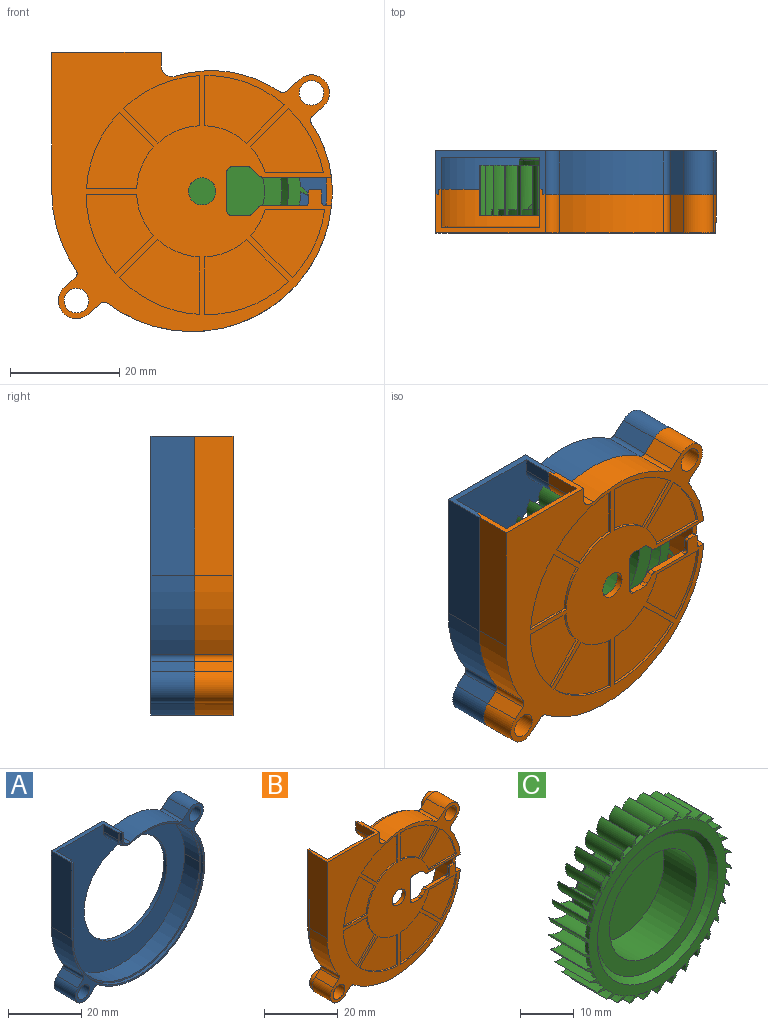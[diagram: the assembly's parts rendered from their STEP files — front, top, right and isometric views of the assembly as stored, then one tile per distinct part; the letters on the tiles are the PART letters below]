
ASSEMBLY  parts=3 mates=2
PART A: 35 faces, bbox 51.3x8x51.1 mm
  f0: cylinder r=25.15mm len=50.3mm, axis (0,-1,0), area 79mm2, adj f28,f32,f33,f34
  f1: cylinder r=2.5mm len=3.25mm, axis (0,-1,0), area 4.7mm2, adj f28,f31,f32,f34
  f2: cylinder r=2.25mm len=8mm, axis (0,1,0), area 113.1mm2, adj f28,f29
  f3: cylinder r=2.25mm len=8mm, axis (0,1,0), area 113.1mm2, adj f28,f29
  f4: cylinder r=22.07mm len=19.05mm, axis (0,1,0), area 159.4mm2, adj f20,f21,f28,f29
  f5: cylinder r=3.3mm len=8mm, axis (0,1,0), area 82.9mm2, adj f18,f19,f28,f29
  f6: cylinder r=1mm len=8mm, axis (0,1,0), area 11mm2, adj f14,f15,f28,f29
  f7: cylinder r=16mm len=32mm, axis (0,1,0), area 120.6mm2, adj f29,f30
  f8: cylinder r=24.65mm len=49.3mm, axis (0,-1,0), area 449.3mm2, adj f11,f12,f30,f34
  f9: cylinder r=3mm len=5.8mm, axis (0,-1,0), area 32.6mm2, adj f10,f11,f30,f34
  f10: plane 5.8x2.44mm, normal (-1,0,0), area 14.2mm2, adj f9,f23,f30,f34
  f11: cylinder r=21.07mm len=27.4mm, axis (0,-1,0), area 229.2mm2, adj f8,f9,f30,f34
  f12: plane 25.4x5.8mm, normal (1,0,0), area 147.3mm2, adj f8,f23,f30,f34
  f13: cylinder r=3.3mm len=8mm, axis (0,1,0), area 82.9mm2, adj f14,f27,f28,f29
  f14: plane 8x2.22mm, normal (0.66,0,-0.75), area 23.7mm2, adj f6,f13,f28,f29
  f15: cylinder r=25.65mm len=41.13mm, axis (0,1,0), area 455.4mm2, adj f6,f16,f28,f29
  f16: cylinder r=22.07mm len=12.41mm, axis (0,1,0), area 105.5mm2, adj f15,f17,f28,f29
  f17: cylinder r=1mm len=8mm, axis (0,1,0), area 11.6mm2, adj f16,f18,f28,f29
  f18: plane 8x2.04mm, normal (0.66,0,-0.75), area 21.8mm2, adj f5,f17,f28,f29
  f19: plane 8x2.44mm, normal (-0.66,0,0.75), area 26mm2, adj f5,f20,f28,f29
  f20: cylinder r=1mm len=8mm, axis (0,1,0), area 10.6mm2, adj f4,f19,f28,f29
  f21: cylinder r=2mm len=8mm, axis (0,1,0), area 30mm2, adj f4,f22,f28,f29
  f22: plane 8x2.44mm, normal (1,0,0), area 19.6mm2, adj f21,f23,f28,f29
  f23: plane 20x8mm, normal (0,0,1), area 36.6mm2, adj f10,f12,f22,f24,f28,f29,f30,f31
  f24: plane 25.4x8mm, normal (-1,0,0), area 203.2mm2, adj f23,f25,f28,f29
  f25: cylinder r=25.65mm len=14.47mm, axis (0,1,0), area 122.9mm2, adj f24,f26,f28,f29
  f26: cylinder r=1mm len=8mm, axis (0,1,0), area 11.6mm2, adj f25,f27,f28,f29
  f27: plane 8x1.98mm, normal (-0.66,0,0.75), area 21.1mm2, adj f13,f26,f28,f29
  f28: plane 51.3x51.07mm, normal (0,-1,0), area 126.8mm2, adj f0,f1,f2,f3,f4,f5,f6,f13
  f29: plane 51.3x51.07mm, normal (0,1,0), area 1370.5mm2, adj f2,f3,f4,f5,f6,f7,f13,f14
  f30: plane 50.07x49.3mm, normal (0,-1,0), area 1168mm2, adj f7,f8,f9,f10,f11,f12,f23
  f31: plane 2.44x1mm, normal (-1,0,0), area 2.4mm2, adj f1,f23,f28,f34
  f32: cylinder r=21.57mm len=28.05mm, axis (0,-1,0), area 40.5mm2, adj f0,f1,f28,f34
  f33: plane 25.4x1mm, normal (1,0,0), area 25.4mm2, adj f0,f23,f28,f34
  f34: plane 50.57x50.3mm, normal (0,-1,0), area 75.6mm2, adj f0,f1,f8,f9,f10,f11,f12,f23
PART B: 104 faces, bbox 52.9x8.5x51.4 mm
  f0: torus R=1.41mm, axis (0,-1,0), area 1.6mm2, adj f31,f35,f102,f103
  f1: cylinder r=21.88mm len=15.3mm, axis (0,-1,0), area 8.4mm2, adj f14,f53,f54,f55
  f2: cylinder r=2.82mm len=5.65mm, axis (0,-1,0), area 26.6mm2, adj f15,f41
  f3: cylinder r=2.82mm len=5.65mm, axis (0,-1,0), area 26.6mm2, adj f15,f40
  f4: cylinder r=21.57mm len=28.05mm, axis (0,1,0), area 40.5mm2, adj f15,f16,f37,f38
  f5: cylinder r=21.07mm len=27.4mm, axis (0,1,0), area 266.7mm2, adj f16,f31,f33,f34,f86,f87
  f6: cylinder r=2.5mm len=5mm, axis (0,-1,0), area 18.8mm2, adj f14,f31
  f7: cylinder r=2.25mm len=8.5mm, axis (0,-1,0), area 120.2mm2, adj f14,f40
  f8: cylinder r=2.25mm len=8.5mm, axis (0,-1,0), area 120.2mm2, adj f14,f41
  f9: cylinder r=25.65mm len=41.13mm, axis (0,-1,0), area 393.3mm2, adj f13,f14,f15,f28,f29,f87
  f10: cylinder r=1mm len=7mm, axis (0,-1,0), area 9.3mm2, adj f14,f15,f23,f24
  f11: cylinder r=2mm len=7mm, axis (0,-1,0), area 26.3mm2, adj f14,f15,f22,f23
  f12: cylinder r=3.3mm len=7mm, axis (0,-1,0), area 72.6mm2, adj f14,f15,f17,f30
  f13: plane 12.66x2mm, normal (0,0,1), area 13.2mm2, adj f9,f14,f31,f34,f87,f93,f95,f98
  f14: plane 51.17x51.07mm, normal (0,-1,0), area 1131.7mm2, adj f1,f6,f7,f8,f9,f10,f11,f12
  f15: plane 51.3x51.07mm, normal (0,1,0), area 108.5mm2, adj f2,f3,f4,f9,f10,f11,f12,f17
  f16: plane 50.57x50.3mm, normal (0,1,0), area 75.6mm2, adj f4,f5,f21,f32,f33,f34,f35,f36
  f17: plane 7x1.98mm, normal (-0.66,0,0.75), area 18.5mm2, adj f12,f14,f15,f18
  f18: cylinder r=1mm len=7mm, axis (0,-1,0), area 10.1mm2, adj f14,f15,f17,f19
  f19: cylinder r=25.65mm len=14.47mm, axis (0,-1,0), area 107.6mm2, adj f14,f15,f18,f20
  f20: plane 25.4x7mm, normal (-1,0,0), area 177.8mm2, adj f14,f15,f19,f21
  f21: plane 20x8mm, normal (0,0,1), area 31.2mm2, adj f14,f15,f16,f20,f22,f32,f35,f36
  f22: plane 7x2.44mm, normal (1,0,0), area 17.1mm2, adj f11,f14,f15,f21
  f23: cylinder r=22.07mm len=19.05mm, axis (0,-1,0), area 139.5mm2, adj f10,f11,f14,f15
  f24: plane 7x2.44mm, normal (-0.66,0,0.75), area 22.8mm2, adj f10,f14,f15,f25
  f25: cylinder r=3.3mm len=7mm, axis (0,-1,0), area 72.6mm2, adj f14,f15,f24,f26
  f26: plane 7x2.04mm, normal (0.66,0,-0.75), area 19.1mm2, adj f14,f15,f25,f27
  f27: cylinder r=1mm len=7mm, axis (0,-1,0), area 10.1mm2, adj f14,f15,f26,f28
  f28: cylinder r=22.07mm len=12.41mm, axis (0,-1,0), area 87.1mm2, adj f9,f14,f15,f27,f86,f87
  f29: cylinder r=1mm len=7mm, axis (0,-1,0), area 9.6mm2, adj f9,f14,f15,f30
  f30: plane 7x2.22mm, normal (0.66,0,-0.75), area 20.7mm2, adj f12,f14,f15,f29
  f31: plane 49.16x46.35mm, normal (0,1,0), area 1650.7mm2, adj f0,f5,f6,f13,f33,f34,f35,f81
  f32: plane 7.1x2.44mm, normal (-1,0,0), area 17.4mm2, adj f16,f21,f33,f102
  f33: cylinder r=3mm len=7.1mm, axis (0,1,0), area 38.5mm2, adj f5,f16,f31,f32,f103
  f34: cylinder r=24.65mm len=49.3mm, axis (0,1,0), area 524.7mm2, adj f5,f13,f16,f31,f35,f87
  f35: plane 25.4x7.1mm, normal (1,0,0), area 179.6mm2, adj f0,f16,f21,f31,f34,f102
  f36: plane 25.4x1mm, normal (-1,0,0), area 25.4mm2, adj f15,f16,f21,f37
  f37: cylinder r=25.15mm len=50.3mm, axis (0,1,0), area 79mm2, adj f4,f15,f16,f36
  f38: cylinder r=2.5mm len=3.25mm, axis (0,1,0), area 4.7mm2, adj f4,f15,f16,f39
  f39: plane 2.44x1mm, normal (1,0,0), area 2.4mm2, adj f15,f16,f21,f38
  f40: plane 5.65x5.65mm, normal (0,1,0), area 9.2mm2, adj f3,f7
  f41: plane 5.65x5.65mm, normal (0,1,0), area 9.2mm2, adj f2,f8
  f42: plane 6.99x6.99mm, normal (0.71,0,-0.71), area 4.9mm2, adj f14,f43,f45,f46
  f43: cylinder r=12mm len=7.62mm, axis (0,-1,0), area 4.2mm2, adj f14,f42,f44,f46
  f44: plane 10.54x0.5mm, normal (-1,0,0), area 5.3mm2, adj f14,f43,f45,f46
  f45: cylinder r=21.88mm len=14.61mm, axis (0,-1,0), area 8.2mm2, adj f14,f42,f44,f46
  f46: plane 14.61x13.7mm, normal (0,-1,0), area 127.2mm2, adj f42,f43,f44,f45
  f47: plane 7.67x7.67mm, normal (0.71,0,0.71), area 5.4mm2, adj f14,f48,f50,f51
  f48: cylinder r=12mm len=4.77mm, axis (0,-1,0), area 2.8mm2, adj f14,f47,f49,f51
  f49: plane 10.88x0.5mm, normal (0,0,-1), area 5.4mm2, adj f14,f48,f50,f51
  f50: cylinder r=21.88mm len=12.45mm, axis (0,-1,0), area 7mm2, adj f14,f47,f49,f51
  f51: plane 13.57x12.45mm, normal (0,-1,0), area 105.4mm2, adj f47,f48,f49,f50
  f52: cylinder r=12mm len=7.62mm, axis (0,-1,0), area 4.2mm2, adj f14,f53,f54,f55
  f53: plane 7.67x7.67mm, normal (-0.71,0,-0.71), area 5.4mm2, adj f1,f14,f52,f55
  f54: plane 10.57x0.5mm, normal (1,0,0), area 5.3mm2, adj f1,f14,f52,f55
  f55: plane 15.3x13.73mm, normal (0,-1,0), area 135.9mm2, adj f1,f52,f53,f54
  f56: cylinder r=12mm len=7.62mm, axis (0,-1,0), area 4.2mm2, adj f14,f57,f59,f60
  f57: plane 9.2x0.5mm, normal (1,0,0), area 4.6mm2, adj f14,f56,f58,f60
  f58: cylinder r=21.88mm len=14.58mm, axis (0,-1,0), area 7.9mm2, adj f14,f57,f59,f60
  f59: plane 6.96x6.96mm, normal (-0.71,0,0.71), area 4.9mm2, adj f14,f56,f58,f60
  f60: plane 14.58x12.36mm, normal (0,-1,0), area 115.4mm2, adj f56,f57,f58,f59
  f61: cylinder r=12mm len=4.77mm, axis (0,-1,0), area 2.8mm2, adj f14,f62,f64,f65
  f62: plane 6.99x6.99mm, normal (0.71,0,-0.71), area 4.9mm2, adj f14,f61,f63,f65
  f63: cylinder r=21.88mm len=11.76mm, axis (0,-1,0), area 6.8mm2, adj f14,f62,f64,f65
  f64: plane 10.66x0.5mm, normal (0,0,1), area 5.3mm2, adj f14,f61,f63,f65
  f65: plane 13.36x11.76mm, normal (0,-1,0), area 97mm2, adj f61,f62,f63,f64
  f66: cylinder r=12mm len=7.62mm, axis (0,-1,0), area 4.2mm2, adj f14,f67,f69,f70
  f67: plane 9.17x0.5mm, normal (0,0,1), area 4.6mm2, adj f14,f66,f68,f70
  f68: cylinder r=21.88mm len=13.93mm, axis (0,-1,0), area 7.7mm2, adj f14,f67,f69,f70
  f69: plane 6.3x6.3mm, normal (-0.71,0,-0.71), area 4.5mm2, adj f14,f66,f68,f70
  f70: plane 13.93x12.33mm, normal (0,-1,0), area 107.6mm2, adj f66,f67,f68,f69
  f71: plane 9.17x0.5mm, normal (-1,0,0), area 4.6mm2, adj f14,f72,f74,f75
  f72: cylinder r=12mm len=7.62mm, axis (0,-1,0), area 4.2mm2, adj f14,f71,f73,f75
  f73: plane 6.3x6.3mm, normal (0.71,0,0.71), area 4.5mm2, adj f14,f72,f74,f75
  f74: cylinder r=21.88mm len=13.93mm, axis (0,-1,0), area 7.7mm2, adj f14,f71,f73,f75
  f75: plane 13.93x12.33mm, normal (0,-1,0), area 107.6mm2, adj f71,f72,f73,f74
  f76: cylinder r=12mm len=7.62mm, axis (0,-1,0), area 4.2mm2, adj f14,f77,f79,f80
  f77: plane 6.96x6.96mm, normal (-0.71,0,0.71), area 4.9mm2, adj f14,f76,f78,f80
  f78: cylinder r=21.88mm len=14.58mm, axis (0,-1,0), area 7.9mm2, adj f14,f77,f79,f80
  f79: plane 9.2x0.5mm, normal (0,0,-1), area 4.6mm2, adj f14,f76,f78,f80
  f80: plane 14.58x12.36mm, normal (0,-1,0), area 115.4mm2, adj f76,f77,f78,f79
  f81: plane 1.31x1.31mm, normal (-0.71,0,0.71), area 2.2mm2, adj f14,f31,f92,f93
  f82: plane 2.79x1.2mm, normal (0,0,1), area 3.3mm2, adj f14,f31,f91,f92
  f83: plane 7x1.2mm, normal (1,0,0), area 8.4mm2, adj f14,f31,f88,f91
  f84: plane 2.79x1.2mm, normal (0,0,-1), area 3.3mm2, adj f14,f31,f88,f90
  f85: plane 1.31x1.31mm, normal (-0.71,0,-0.71), area 2.2mm2, adj f14,f31,f89,f90
  f86: plane 12.63x2mm, normal (0,0,-1), area 16mm2, adj f5,f14,f28,f31,f87,f89
  f87: plane 5.2x1.16mm, normal (0,-1,0), area 5.2mm2, adj f5,f9,f13,f28,f34,f86
  f88: cylinder r=1mm len=1.2mm, axis (0,1,0), area 1.9mm2, adj f14,f31,f83,f84
  f89: cylinder r=1mm len=1.2mm, axis (0,-1,0), area 0.9mm2, adj f14,f31,f85,f86
  f90: cylinder r=1mm len=1.2mm, axis (0,1,0), area 0.9mm2, adj f14,f31,f84,f85
  f91: cylinder r=1mm len=1.2mm, axis (0,1,0), area 1.9mm2, adj f14,f31,f82,f83
  f92: cylinder r=1mm len=1.2mm, axis (0,1,0), area 0.9mm2, adj f14,f31,f81,f82
  f93: cylinder r=1mm len=1.2mm, axis (0,-1,0), area 0.9mm2, adj f13,f14,f31,f81
  f94: plane 2x0.8mm, normal (1,0,0), area 1.6mm2, adj f14,f95,f100,f101
  f95: plane 3.5x3mm, normal (0,1,0), area 7.5mm2, adj f13,f94,f96,f97,f98,f99,f100,f101
  f96: plane 2x0.8mm, normal (-1,0,0), area 1.6mm2, adj f14,f95,f98,f99
  f97: plane 1.5x0.8mm, normal (0,0,1), area 1.2mm2, adj f14,f95,f99,f100
  f98: cylinder r=0.5mm len=0.8mm, axis (0,1,0), area 0.6mm2, adj f13,f14,f95,f96
  f99: cylinder r=0.5mm len=0.8mm, axis (0,1,0), area 0.6mm2, adj f14,f95,f96,f97
  f100: cylinder r=0.5mm len=0.8mm, axis (0,-1,0), area 0.6mm2, adj f14,f94,f95,f97
  f101: cylinder r=0.5mm len=0.8mm, axis (0,-1,0), area 0.6mm2, adj f13,f14,f94,f95
  f102: plane 22.44x18mm, normal (0,1,0), area 150.3mm2, adj f0,f21,f32,f35,f103
  f103: torus R=22.35mm, axis (0,1,0), area 37.3mm2, adj f0,f31,f33,f102
PART C: 207 faces, bbox 39x10.5x38.9 mm
  f0: cylinder r=11.4mm len=22.8mm, axis (0,-1,0), area 608.8mm2, adj f205,f206
  f1: cone r=14.6mm half-angle=45deg, axis (0,-1,0), area 162.1mm2, adj f119,f205
  f2: cylinder r=2.92mm len=9.2mm, axis (0,-1,0), area 52mm2, adj f85,f86,f87,f119,f143,f144
  f3: cylinder r=2.92mm len=9.2mm, axis (0,-1,0), area 52mm2, adj f88,f89,f90,f119,f141,f142
  f4: cylinder r=2.92mm len=9.2mm, axis (0,-1,0), area 52mm2, adj f91,f92,f93,f119,f139,f140
  f5: cylinder r=5.73mm len=9.2mm, axis (0,-1,0), area 44mm2, adj f6,f91,f92,f93,f119,f138
  f6: cylinder r=2.92mm len=9.2mm, axis (0,-1,0), area 52mm2, adj f5,f94,f95,f96,f119,f138
  f7: cylinder r=5.73mm len=9.2mm, axis (0,-1,0), area 44mm2, adj f8,f94,f95,f96,f119,f137
  f8: cylinder r=2.92mm len=9.2mm, axis (0,-1,0), area 52mm2, adj f7,f97,f98,f99,f119,f137
  f9: cylinder r=5.73mm len=9.2mm, axis (0,-1,0), area 44mm2, adj f10,f97,f98,f99,f119,f136
  f10: cylinder r=2.92mm len=9.2mm, axis (0,-1,0), area 52mm2, adj f9,f100,f101,f102,f119,f136
  f11: cylinder r=5.73mm len=9.2mm, axis (0,-1,0), area 44mm2, adj f12,f100,f101,f102,f119,f135
  f12: cylinder r=2.92mm len=9.2mm, axis (0,-1,0), area 52mm2, adj f11,f103,f104,f105,f119,f135
  f13: cylinder r=5.73mm len=9.2mm, axis (0,-1,0), area 44mm2, adj f14,f103,f104,f105,f119,f134
  f14: cylinder r=2.92mm len=9.2mm, axis (0,-1,0), area 52mm2, adj f13,f106,f107,f108,f119,f134
  f15: cylinder r=2.92mm len=9.2mm, axis (0,-1,0), area 52mm2, adj f109,f110,f111,f119,f132,f133
  f16: cylinder r=2.92mm len=9.2mm, axis (0,-1,0), area 52mm2, adj f112,f113,f114,f119,f130,f131
  f17: cylinder r=2.92mm len=9.2mm, axis (0,-1,0), area 52mm2, adj f115,f116,f117,f119,f128,f129
  f18: torus R=11.75mm, axis (0,1,0), area 59.6mm2, adj f19,f121
  f19: cylinder r=12.25mm len=24.5mm, axis (0,-1,0), area 577.3mm2, adj f18,f120
  f20: cone r=14.5mm half-angle=45deg, axis (0,-1,0), area 5.5mm2, adj f118,f120,f123,f125
  f21: cylinder r=18mm len=2.51mm, axis (0,-1,0), area 2.5mm2, adj f118,f119,f123,f125
  f22: cylinder r=18mm len=2.35mm, axis (0,-1,0), area 2.5mm2, adj f24,f119,f200,f202
  f23: cylinder r=18mm len=2.47mm, axis (0,-1,0), area 2.5mm2, adj f25,f119,f122,f203
  f24: plane 2.87x2.61mm, normal (0,1,0), area 4.7mm2, adj f22,f26,f200,f202
  f25: plane 2.53x2.46mm, normal (0,1,0), area 4.7mm2, adj f23,f27,f122,f203
  f26: cone r=14.5mm half-angle=45deg, axis (0,-1,0), area 5.5mm2, adj f24,f120,f200,f202
  f27: cone r=14.5mm half-angle=45deg, axis (0,-1,0), area 5.5mm2, adj f25,f120,f122,f203
  f28: cylinder r=18mm len=2.14mm, axis (0,-1,0), area 2.5mm2, adj f29,f119,f197,f199
  f29: plane 3.17x2.78mm, normal (0,1,0), area 4.7mm2, adj f28,f30,f197,f199
  f30: cone r=14.5mm half-angle=45deg, axis (0,-1,0), area 5.5mm2, adj f29,f120,f197,f199
  f31: cylinder r=18mm len=1.86mm, axis (0,-1,0), area 2.5mm2, adj f32,f119,f194,f196
  f32: plane 3.37x2.85mm, normal (0,1,0), area 4.7mm2, adj f31,f33,f194,f196
  f33: cone r=14.5mm half-angle=45deg, axis (0,-1,0), area 5.5mm2, adj f32,f120,f194,f196
  f34: cylinder r=18mm len=2.01mm, axis (0,-1,0), area 2.5mm2, adj f35,f119,f191,f193
  f35: plane 3.44x2.81mm, normal (0,1,0), area 4.7mm2, adj f34,f36,f191,f193
  f36: cone r=14.5mm half-angle=45deg, axis (0,-1,0), area 5.5mm2, adj f35,f120,f191,f193
  f37: cylinder r=18mm len=2.25mm, axis (0,-1,0), area 2.5mm2, adj f38,f119,f188,f190
  f38: plane 3.38x2.68mm, normal (0,1,0), area 4.7mm2, adj f37,f39,f188,f190
  f39: cone r=14.5mm half-angle=45deg, axis (0,-1,0), area 5.5mm2, adj f38,f120,f188,f190
  f40: cylinder r=18mm len=2.42mm, axis (0,-1,0), area 2.5mm2, adj f41,f119,f185,f187
  f41: plane 3.21x2.44mm, normal (0,1,0), area 4.7mm2, adj f40,f42,f185,f187
  f42: cone r=14.5mm half-angle=45deg, axis (0,-1,0), area 5.5mm2, adj f41,f120,f185,f187
  f43: cylinder r=18mm len=2.5mm, axis (0,-1,0), area 2.5mm2, adj f44,f119,f182,f184
  f44: plane 2.92x2.12mm, normal (0,1,0), area 4.7mm2, adj f43,f45,f182,f184
  f45: cone r=14.5mm half-angle=45deg, axis (0,-1,0), area 5.5mm2, adj f44,f120,f182,f184
  f46: cylinder r=18mm len=2.49mm, axis (0,-1,0), area 2.5mm2, adj f47,f119,f179,f181
  f47: plane 2.6x2.34mm, normal (0,1,0), area 4.7mm2, adj f46,f48,f179,f181
  f48: cone r=14.5mm half-angle=45deg, axis (0,-1,0), area 5.5mm2, adj f47,f120,f179,f181
  f49: cylinder r=18mm len=2.39mm, axis (0,-1,0), area 2.5mm2, adj f50,f119,f176,f178
  f50: plane 2.77x2.56mm, normal (0,1,0), area 4.7mm2, adj f49,f51,f176,f178
  f51: cone r=14.5mm half-angle=45deg, axis (0,-1,0), area 5.5mm2, adj f50,f120,f176,f178
  f52: cylinder r=18mm len=2.2mm, axis (0,-1,0), area 2.5mm2, adj f53,f119,f173,f175
  f53: plane 3.11x2.75mm, normal (0,1,0), area 4.7mm2, adj f52,f54,f173,f175
  f54: cone r=14.5mm half-angle=45deg, axis (0,-1,0), area 5.5mm2, adj f53,f120,f173,f175
  f55: cylinder r=18mm len=1.94mm, axis (0,-1,0), area 2.5mm2, adj f56,f119,f170,f172
  f56: plane 3.33x2.84mm, normal (0,1,0), area 4.7mm2, adj f55,f57,f170,f172
  f57: cone r=14.5mm half-angle=45deg, axis (0,-1,0), area 5.5mm2, adj f56,f120,f170,f172
  f58: cylinder r=18mm len=1.93mm, axis (0,-1,0), area 2.5mm2, adj f59,f119,f167,f169
  f59: plane 3.43x2.83mm, normal (0,1,0), area 4.7mm2, adj f58,f60,f167,f169
  f60: cone r=14.5mm half-angle=45deg, axis (0,-1,0), area 5.5mm2, adj f59,f120,f167,f169
  f61: cylinder r=18mm len=2.2mm, axis (0,-1,0), area 2.5mm2, adj f62,f119,f164,f166
  f62: plane 3.41x2.72mm, normal (0,1,0), area 4.7mm2, adj f61,f63,f164,f166
  f63: cone r=14.5mm half-angle=45deg, axis (0,-1,0), area 5.5mm2, adj f62,f120,f164,f166
  f64: cylinder r=18mm len=2.39mm, axis (0,-1,0), area 2.5mm2, adj f65,f119,f161,f163
  f65: plane 3.26x2.51mm, normal (0,1,0), area 4.7mm2, adj f64,f66,f161,f163
  f66: cone r=14.5mm half-angle=45deg, axis (0,-1,0), area 5.5mm2, adj f65,f120,f161,f163
  f67: cylinder r=18mm len=2.49mm, axis (0,-1,0), area 2.5mm2, adj f68,f119,f158,f160
  f68: plane 3x2.21mm, normal (0,1,0), area 4.7mm2, adj f67,f69,f158,f160
  f69: cone r=14.5mm half-angle=45deg, axis (0,-1,0), area 5.5mm2, adj f68,f120,f158,f160
  f70: cylinder r=18mm len=2.5mm, axis (0,-1,0), area 2.5mm2, adj f71,f119,f155,f157
  f71: plane 2.67x2.22mm, normal (0,1,0), area 4.7mm2, adj f70,f72,f155,f157
  f72: cone r=14.5mm half-angle=45deg, axis (0,-1,0), area 5.5mm2, adj f71,f120,f155,f157
  f73: cylinder r=18mm len=2.42mm, axis (0,-1,0), area 2.5mm2, adj f74,f119,f152,f154
  f74: plane 2.67x2.5mm, normal (0,1,0), area 4.7mm2, adj f73,f75,f152,f154
  f75: cone r=14.5mm half-angle=45deg, axis (0,-1,0), area 5.5mm2, adj f74,f120,f152,f154
  f76: cylinder r=18mm len=2.26mm, axis (0,-1,0), area 2.5mm2, adj f77,f119,f149,f151
  f77: plane 3.04x2.71mm, normal (0,1,0), area 4.7mm2, adj f76,f78,f149,f151
  f78: cone r=14.5mm half-angle=45deg, axis (0,-1,0), area 5.5mm2, adj f77,f120,f149,f151
  f79: cylinder r=18mm len=2.01mm, axis (0,-1,0), area 2.5mm2, adj f80,f119,f146,f148
  f80: plane 3.29x2.83mm, normal (0,1,0), area 4.7mm2, adj f79,f81,f146,f148
  f81: cone r=14.5mm half-angle=45deg, axis (0,-1,0), area 5.5mm2, adj f80,f120,f146,f148
  f82: cylinder r=18mm len=1.85mm, axis (0,-1,0), area 2.5mm2, adj f83,f119,f143,f145
  f83: plane 3.42x2.84mm, normal (0,1,0), area 4.7mm2, adj f82,f84,f143,f145
  f84: cone r=14.5mm half-angle=45deg, axis (0,-1,0), area 5.5mm2, adj f83,f120,f143,f145
  f85: cylinder r=18mm len=2.14mm, axis (0,-1,0), area 2.5mm2, adj f2,f86,f119,f141
  f86: plane 3.43x2.76mm, normal (0,1,0), area 4.7mm2, adj f2,f85,f87,f141
  f87: cone r=14.5mm half-angle=45deg, axis (0,-1,0), area 5.3mm2, adj f2,f86,f120,f141
  f88: cylinder r=18mm len=2.35mm, axis (0,-1,0), area 2.5mm2, adj f3,f89,f119,f139
  f89: plane 3.31x2.57mm, normal (0,1,0), area 4.7mm2, adj f3,f88,f90,f139
  f90: cone r=14.5mm half-angle=45deg, axis (0,-1,0), area 5.3mm2, adj f3,f89,f120,f139
  f91: cylinder r=18mm len=2.47mm, axis (0,-1,0), area 2.5mm2, adj f4,f5,f92,f119
  f92: plane 3.08x2.29mm, normal (0,1,0), area 4.7mm2, adj f4,f5,f91,f93
  f93: cone r=14.5mm half-angle=45deg, axis (0,-1,0), area 5.2mm2, adj f4,f5,f92,f120
  f94: cylinder r=18mm len=2.51mm, axis (0,-1,0), area 2.5mm2, adj f6,f7,f95,f119
  f95: plane 2.74x2.11mm, normal (0,1,0), area 4.7mm2, adj f6,f7,f94,f96
  f96: cone r=14.5mm half-angle=45deg, axis (0,-1,0), area 5.5mm2, adj f6,f7,f95,f120
  f97: cylinder r=18mm len=2.45mm, axis (0,-1,0), area 2.5mm2, adj f8,f9,f98,f119
  f98: plane 2.57x2.48mm, normal (0,1,0), area 4.7mm2, adj f8,f9,f97,f99
  f99: cone r=14.5mm half-angle=45deg, axis (0,-1,0), area 5.5mm2, adj f8,f9,f98,f120
  f100: cylinder r=18mm len=2.31mm, axis (0,-1,0), area 2.5mm2, adj f10,f11,f101,f119
  f101: plane 2.96x2.66mm, normal (0,1,0), area 4.7mm2, adj f10,f11,f100,f102
  f102: cone r=14.5mm half-angle=45deg, axis (0,-1,0), area 5.5mm2, adj f10,f11,f101,f120
  f103: cylinder r=18mm len=2.08mm, axis (0,-1,0), area 2.5mm2, adj f12,f13,f104,f119
  f104: plane 3.23x2.81mm, normal (0,1,0), area 4.7mm2, adj f12,f13,f103,f105
  f105: cone r=14.5mm half-angle=45deg, axis (0,-1,0), area 5.5mm2, adj f12,f13,f104,f120
  f106: cylinder r=18mm len=1.78mm, axis (0,-1,0), area 2.5mm2, adj f14,f107,f119,f132
  f107: plane 3.4x2.85mm, normal (0,1,0), area 4.7mm2, adj f14,f106,f108,f132
  f108: cone r=14.5mm half-angle=45deg, axis (0,-1,0), area 5.5mm2, adj f14,f107,f120,f132
  f109: cylinder r=18mm len=2.08mm, axis (0,-1,0), area 2.5mm2, adj f15,f110,f119,f130
  f110: plane 3.44x2.79mm, normal (0,1,0), area 4.7mm2, adj f15,f109,f111,f130
  f111: cone r=14.5mm half-angle=45deg, axis (0,-1,0), area 5.5mm2, adj f15,f110,f120,f130
  f112: cylinder r=18mm len=2.3mm, axis (0,-1,0), area 2.5mm2, adj f16,f113,f119,f128
  f113: plane 3.35x2.63mm, normal (0,1,0), area 4.7mm2, adj f16,f112,f114,f128
  f114: cone r=14.5mm half-angle=45deg, axis (0,-1,0), area 5.5mm2, adj f16,f113,f120,f128
  f115: cylinder r=18mm len=2.45mm, axis (0,-1,0), area 2.5mm2, adj f17,f116,f119,f126
  f116: plane 3.14x2.37mm, normal (0,1,0), area 4.7mm2, adj f17,f115,f117,f126
  f117: cone r=14.5mm half-angle=45deg, axis (0,-1,0), area 5.5mm2, adj f17,f116,f120,f126
  f118: plane 2.83x2.05mm, normal (0,1,0), area 4.7mm2, adj f20,f21,f123,f125
  f119: plane 38.96x38.91mm, normal (0,-1,0), area 265.7mm2, adj f1,f2,f3,f4,f5,f6,f7,f8
  f120: plane 29x29mm, normal (0,1,0), area 189.1mm2, adj f19,f20,f26,f27,f30,f33,f36,f39
  f121: plane 23.5x23.5mm, normal (0,1,0), area 433.7mm2, adj f18
  f122: cylinder r=2.92mm len=9.2mm, axis (0,-1,0), area 52mm2, adj f23,f25,f27,f119,f123,f124
  f123: cylinder r=5.73mm len=9.2mm, axis (0,-1,0), area 44mm2, adj f20,f21,f118,f119,f122,f124
  f124: plane 5.03x1.97mm, normal (0,1,0), area 3.4mm2, adj f122,f123
  f125: cylinder r=2.92mm len=9.2mm, axis (0,-1,0), area 52mm2, adj f20,f21,f118,f119,f126,f127
  f126: cylinder r=5.73mm len=9.2mm, axis (0,-1,0), area 44mm2, adj f115,f116,f117,f119,f125,f127
  f127: plane 4.77x2.5mm, normal (0,1,0), area 3.4mm2, adj f125,f126
  f128: cylinder r=5.73mm len=9.2mm, axis (0,-1,0), area 44mm2, adj f17,f112,f113,f114,f119,f129
  f129: plane 4.34x3.06mm, normal (0,1,0), area 3.4mm2, adj f17,f128
  f130: cylinder r=5.73mm len=9.2mm, axis (0,-1,0), area 44mm2, adj f16,f109,f110,f111,f119,f131
  f131: plane 3.83x3.61mm, normal (0,1,0), area 3.4mm2, adj f16,f130
  f132: cylinder r=5.73mm len=9.2mm, axis (0,-1,0), area 44mm2, adj f15,f106,f107,f108,f119,f133
  f133: plane 4.13x3.29mm, normal (0,1,0), area 3.4mm2, adj f15,f132
  f134: plane 4.61x2.74mm, normal (0,1,0), area 3.4mm2, adj f13,f14
  f135: plane 4.94x2.19mm, normal (0,1,0), area 3.4mm2, adj f11,f12
  f136: plane 5.09x1.66mm, normal (0,1,0), area 3.4mm2, adj f9,f10
  f137: plane 5.06x1.83mm, normal (0,1,0), area 3.4mm2, adj f7,f8
  f138: plane 4.85x2.37mm, normal (0,1,0), area 3.4mm2, adj f5,f6
  f139: cylinder r=5.73mm len=9.2mm, axis (0,-1,0), area 44mm2, adj f4,f88,f89,f90,f119,f140
  f140: plane 4.46x2.92mm, normal (0,1,0), area 3.4mm2, adj f4,f139
  f141: cylinder r=5.73mm len=9.2mm, axis (0,-1,0), area 44mm2, adj f3,f85,f86,f87,f119,f142
  f142: plane 3.96x3.47mm, normal (0,1,0), area 3.4mm2, adj f3,f141
  f143: cylinder r=5.73mm len=9.2mm, axis (0,-1,0), area 44mm2, adj f2,f82,f83,f84,f119,f144
  f144: plane 4.01x3.43mm, normal (0,1,0), area 3.4mm2, adj f2,f143
  f145: cylinder r=2.92mm len=9.2mm, axis (0,-1,0), area 52mm2, adj f82,f83,f84,f119,f146,f147
  f146: cylinder r=5.73mm len=9.2mm, axis (0,-1,0), area 44mm2, adj f79,f80,f81,f119,f145,f147
  f147: plane 4.5x2.87mm, normal (0,1,0), area 3.4mm2, adj f145,f146
  f148: cylinder r=2.92mm len=9.2mm, axis (0,-1,0), area 52mm2, adj f79,f80,f81,f119,f149,f150
  f149: cylinder r=5.73mm len=9.2mm, axis (0,-1,0), area 44mm2, adj f76,f77,f78,f119,f148,f150
  f150: plane 4.87x2.32mm, normal (0,1,0), area 3.4mm2, adj f148,f149
  f151: cylinder r=2.92mm len=9.2mm, axis (0,-1,0), area 52mm2, adj f76,f77,f78,f119,f152,f153
  f152: cylinder r=5.73mm len=9.2mm, axis (0,-1,0), area 44mm2, adj f73,f74,f75,f119,f151,f153
  f153: plane 5.07x1.79mm, normal (0,1,0), area 3.4mm2, adj f151,f152
  f154: cylinder r=2.92mm len=9.2mm, axis (0,-1,0), area 52mm2, adj f73,f74,f75,f119,f155,f156
  f155: cylinder r=5.73mm len=9.2mm, axis (0,-1,0), area 44mm2, adj f70,f71,f72,f119,f154,f156
  f156: plane 5.09x1.71mm, normal (0,1,0), area 3.4mm2, adj f154,f155
  f157: cylinder r=2.92mm len=9.2mm, axis (0,-1,0), area 52mm2, adj f70,f71,f72,f119,f158,f159
  f158: cylinder r=5.73mm len=9.2mm, axis (0,-1,0), area 44mm2, adj f67,f68,f69,f119,f157,f159
  f159: plane 4.92x2.23mm, normal (0,1,0), area 3.4mm2, adj f157,f158
  f160: cylinder r=2.92mm len=9.2mm, axis (0,-1,0), area 52mm2, adj f67,f68,f69,f119,f161,f162
  f161: cylinder r=5.73mm len=9.2mm, axis (0,-1,0), area 44mm2, adj f64,f65,f66,f119,f160,f162
  f162: plane 4.57x2.78mm, normal (0,1,0), area 3.4mm2, adj f160,f161
  f163: cylinder r=2.92mm len=9.2mm, axis (0,-1,0), area 52mm2, adj f64,f65,f66,f119,f164,f165
  f164: cylinder r=5.73mm len=9.2mm, axis (0,-1,0), area 44mm2, adj f61,f62,f63,f119,f163,f165
  f165: plane 4.09x3.34mm, normal (0,1,0), area 3.4mm2, adj f163,f164
  f166: cylinder r=2.92mm len=9.2mm, axis (0,-1,0), area 52mm2, adj f61,f62,f63,f119,f167,f168
  f167: cylinder r=5.73mm len=9.2mm, axis (0,-1,0), area 44mm2, adj f58,f59,f60,f119,f166,f168
  f168: plane 3.88x3.56mm, normal (0,1,0), area 3.4mm2, adj f166,f167
  f169: cylinder r=2.92mm len=9.2mm, axis (0,-1,0), area 52mm2, adj f58,f59,f60,f119,f170,f171
  f170: cylinder r=5.73mm len=9.2mm, axis (0,-1,0), area 44mm2, adj f55,f56,f57,f119,f169,f171
  f171: plane 4.38x3.01mm, normal (0,1,0), area 3.4mm2, adj f169,f170
  f172: cylinder r=2.92mm len=9.2mm, axis (0,-1,0), area 52mm2, adj f55,f56,f57,f119,f173,f174
  f173: cylinder r=5.73mm len=9.2mm, axis (0,-1,0), area 44mm2, adj f52,f53,f54,f119,f172,f174
  f174: plane 4.8x2.46mm, normal (0,1,0), area 3.4mm2, adj f172,f173
  f175: cylinder r=2.92mm len=9.2mm, axis (0,-1,0), area 52mm2, adj f52,f53,f54,f119,f176,f177
  f176: cylinder r=5.73mm len=9.2mm, axis (0,-1,0), area 44mm2, adj f49,f50,f51,f119,f175,f177
  f177: plane 5.04x1.92mm, normal (0,1,0), area 3.4mm2, adj f175,f176
  f178: cylinder r=2.92mm len=9.2mm, axis (0,-1,0), area 52mm2, adj f49,f50,f51,f119,f179,f180
  f179: cylinder r=5.73mm len=9.2mm, axis (0,-1,0), area 44mm2, adj f46,f47,f48,f119,f178,f180
  f180: plane 5.1x1.58mm, normal (0,1,0), area 3.4mm2, adj f178,f179
  f181: cylinder r=2.92mm len=9.2mm, axis (0,-1,0), area 52mm2, adj f46,f47,f48,f119,f182,f183
  f182: cylinder r=5.73mm len=9.2mm, axis (0,-1,0), area 44mm2, adj f43,f44,f45,f119,f181,f183
  f183: plane 4.98x2.1mm, normal (0,1,0), area 3.4mm2, adj f181,f182
  f184: cylinder r=2.92mm len=9.2mm, axis (0,-1,0), area 52mm2, adj f43,f44,f45,f119,f185,f186
  f185: cylinder r=5.73mm len=9.2mm, axis (0,-1,0), area 44mm2, adj f40,f41,f42,f119,f184,f186
  f186: plane 4.68x2.64mm, normal (0,1,0), area 3.4mm2, adj f184,f185
  f187: cylinder r=2.92mm len=9.2mm, axis (0,-1,0), area 52mm2, adj f40,f41,f42,f119,f188,f189
  f188: cylinder r=5.73mm len=9.2mm, axis (0,-1,0), area 44mm2, adj f37,f38,f39,f119,f187,f189
  f189: plane 4.22x3.2mm, normal (0,1,0), area 3.4mm2, adj f187,f188
  f190: cylinder r=2.92mm len=9.2mm, axis (0,-1,0), area 52mm2, adj f37,f38,f39,f119,f191,f192
  f191: cylinder r=5.73mm len=9.2mm, axis (0,-1,0), area 44mm2, adj f34,f35,f36,f119,f190,f192
  f192: plane 3.74x3.7mm, normal (0,1,0), area 3.4mm2, adj f190,f191
  f193: cylinder r=2.92mm len=9.2mm, axis (0,-1,0), area 52mm2, adj f34,f35,f36,f119,f194,f195
  f194: cylinder r=5.73mm len=9.2mm, axis (0,-1,0), area 44mm2, adj f31,f32,f33,f119,f193,f195
  f195: plane 4.26x3.15mm, normal (0,1,0), area 3.4mm2, adj f193,f194
  f196: cylinder r=2.92mm len=9.2mm, axis (0,-1,0), area 52mm2, adj f31,f32,f33,f119,f197,f198
  f197: cylinder r=5.73mm len=9.2mm, axis (0,-1,0), area 44mm2, adj f28,f29,f30,f119,f196,f198
  f198: plane 4.71x2.6mm, normal (0,1,0), area 3.4mm2, adj f196,f197
  f199: cylinder r=2.92mm len=9.2mm, axis (0,-1,0), area 52mm2, adj f28,f29,f30,f119,f200,f201
  f200: cylinder r=5.73mm len=9.2mm, axis (0,-1,0), area 44mm2, adj f22,f24,f26,f119,f199,f201
  f201: plane 5x2.05mm, normal (0,1,0), area 3.4mm2, adj f199,f200
  f202: cylinder r=2.92mm len=9.2mm, axis (0,-1,0), area 52mm2, adj f22,f24,f26,f119,f203,f204
  f203: cylinder r=5.73mm len=9.2mm, axis (0,-1,0), area 44mm2, adj f23,f25,f27,f119,f202,f204
  f204: plane 5.1x1.54mm, normal (0,1,0), area 3.4mm2, adj f202,f203
  f205: plane 29.2x29.2mm, normal (0,-1,0), area 261.4mm2, adj f0,f1
  f206: plane 22.8x22.8mm, normal (0,-1,0), area 408.3mm2, adj f0
PLACE A t=(-10.45,8.59,-1.09)mm
PLACE B t=(-10.45,-6.41,-1.09)mm
PLACE C rot(axis=(0,1,0),0deg) t=(-10.45,-3.21,-1.09)mm
MATE revolute C.f0 <-> B.f6  axis (0,1,0) through (-10.45,-3.21,-1.09)mm
MATE fastened A.f28 <-> B.f15  axis (0,-1,0) through (-37.95,0.59,11.61)mm
